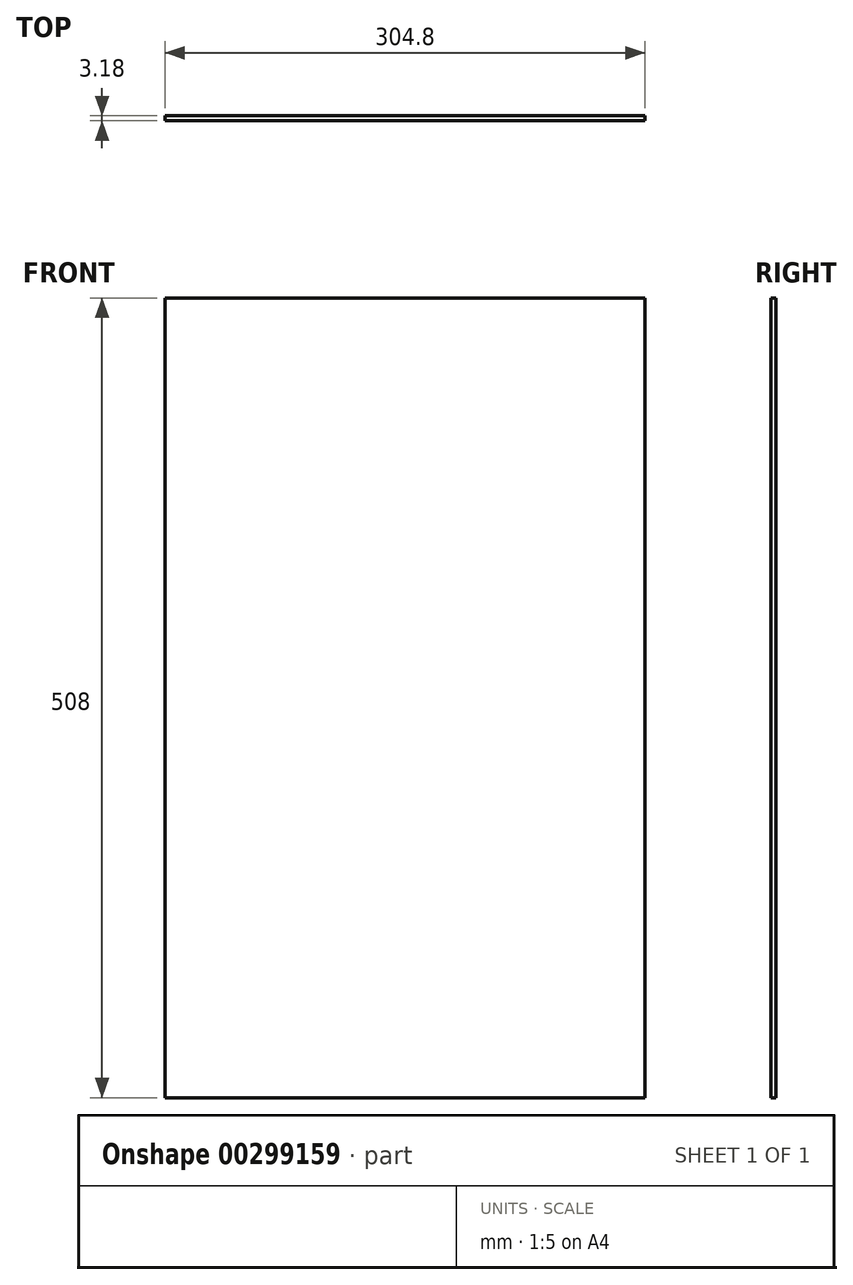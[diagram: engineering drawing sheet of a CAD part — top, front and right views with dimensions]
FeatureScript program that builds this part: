
annotation { "Feature Type Name" : "Feature", "Feature Type Description" : "" }
export const myFeature = defineFeature(function(context is Context, id is Id, definition is map)
    precondition{}
    {
        {
            var Q0;
            Q0=qCreatedBy(makeId("Front.planeOp"),FACE);
            var sketch = newSketch(context, id + "F0", { "sketchPlane" : qUnion([Q0])});
            skLineSegment(sketch, "E0.bottom", {"start": v(-152.4, 254) * mm, "end": v(152.4, 254) * mm});
            skLineSegment(sketch, "E0.top", {"start": v(-152.4, -254) * mm, "end": v(152.4, -254) * mm});
            skLineSegment(sketch, "E0.left", {"start": v(-152.4, 254) * mm, "end": v(-152.4, -254) * mm});
            skLineSegment(sketch, "E0.right", {"start": v(152.4, 254) * mm, "end": v(152.4, -254) * mm});
            skPoint(sketch, "E0.middle", {"position": v(0, 0) * mm});
            skSolve(sketch);
        }
        {
            var Q0;
            Q0 = qSketchRegion(id + "F0", true);
            extrude(context, id + "F1", {"entities" : qUnion([Q0]), "endBound" : BoundingType.SYMMETRIC, "depth" : 3.17 * mm});
        }
    });
